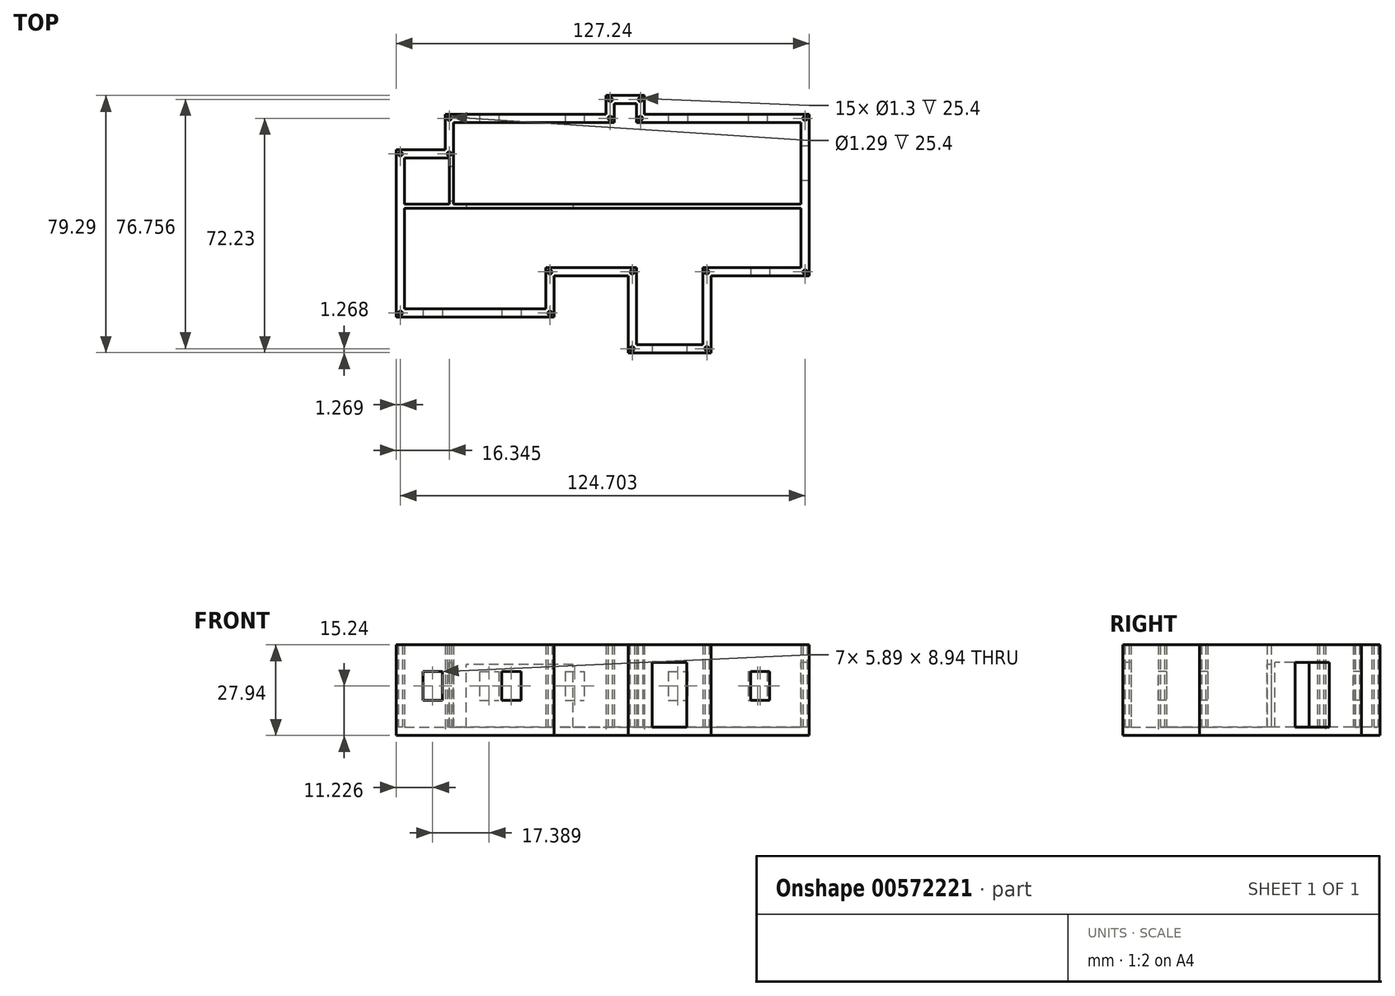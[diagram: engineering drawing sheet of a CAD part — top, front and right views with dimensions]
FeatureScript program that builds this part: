
annotation { "Feature Type Name" : "Feature", "Feature Type Description" : "" }
export const myFeature = defineFeature(function(context is Context, id is Id, definition is map)
    precondition{}
    {
        {
            var Q0;
            Q0=qCreatedBy(makeId("Top.planeOp"),FACE);
            var sketch = newSketch(context, id + "F0", { "sketchPlane" : qUnion([Q0])});
            skLineSegment(sketch, "E0", {"start": v(-47.94, 2.54) * mm, "end": v(1.67, 2.54) * mm});
            skLineSegment(sketch, "E1", {"start": v(1.67, 2.54) * mm, "end": v(1.67, 8.33) * mm});
            skLineSegment(sketch, "E2", {"start": v(1.67, 8.33) * mm, "end": v(13.5, 8.33) * mm});
            skLineSegment(sketch, "E3", {"start": v(13.5, 8.33) * mm, "end": v(13.5, 2.54) * mm});
            skLineSegment(sketch, "E4", {"start": v(13.5, 2.54) * mm, "end": v(64.22, 2.54) * mm});
            skLineSegment(sketch, "E5", {"start": v(-47.94, 2.54) * mm, "end": v(-47.94, -8.42) * mm});
            skLineSegment(sketch, "E6", {"start": v(-47.94, -8.42) * mm, "end": v(-63.02, -8.42) * mm});
            skLineSegment(sketch, "E7", {"start": v(-63.02, -8.42) * mm, "end": v(-63.02, -60.04) * mm});
            skLineSegment(sketch, "E8", {"start": v(-63.02, -60.04) * mm, "end": v(-14.4, -60.04) * mm});
            skLineSegment(sketch, "E9", {"start": v(-14.4, -60.04) * mm, "end": v(-14.4, -47.34) * mm});
            skLineSegment(sketch, "E10", {"start": v(-14.4, -47.34) * mm, "end": v(8.42, -47.34) * mm});
            skLineSegment(sketch, "E11", {"start": v(8.42, -47.34) * mm, "end": v(8.42, -70.96) * mm});
            skLineSegment(sketch, "E12", {"start": v(8.42, -70.96) * mm, "end": v(33.96, -70.96) * mm});
            skLineSegment(sketch, "E13", {"start": v(33.96, -70.96) * mm, "end": v(33.96, -47.34) * mm});
            skLineSegment(sketch, "E14", {"start": v(33.96, -47.34) * mm, "end": v(64.22, -47.34) * mm});
            skLineSegment(sketch, "E15", {"start": v(64.22, -47.34) * mm, "end": v(64.22, 2.54) * mm});
            skLineSegment(sketch, "E16", {"start": v(10.96, -47.34) * mm, "end": v(10.96, -68.42) * mm});
            skLineSegment(sketch, "E17", {"start": v(10.96, -68.42) * mm, "end": v(31.42, -68.42) * mm});
            skLineSegment(sketch, "E18", {"start": v(31.42, -68.42) * mm, "end": v(31.42, -44.8) * mm});
            skLineSegment(sketch, "E19", {"start": v(31.42, -44.8) * mm, "end": v(61.68, -44.8) * mm});
            skLineSegment(sketch, "E20", {"start": v(61.68, -44.8) * mm, "end": v(61.68, 0) * mm});
            skLineSegment(sketch, "E21", {"start": v(61.68, 0) * mm, "end": v(10.96, 0) * mm});
            skLineSegment(sketch, "E22", {"start": v(10.96, 0) * mm, "end": v(10.96, 5.8) * mm});
            skLineSegment(sketch, "E23", {"start": v(10.96, 5.8) * mm, "end": v(4.2, 5.8) * mm});
            skLineSegment(sketch, "E24", {"start": v(4.2, 5.8) * mm, "end": v(4.2, 0) * mm});
            skLineSegment(sketch, "E25", {"start": v(4.2, 0) * mm, "end": v(-45.4, 0) * mm});
            skLineSegment(sketch, "E26", {"start": v(-45.4, 0) * mm, "end": v(-45.4, -10.96) * mm});
            skLineSegment(sketch, "E27", {"start": v(-45.4, -10.96) * mm, "end": v(-60.48, -10.96) * mm});
            skLineSegment(sketch, "E28", {"start": v(-60.48, -10.96) * mm, "end": v(-60.48, -57.5) * mm});
            skLineSegment(sketch, "E29", {"start": v(-60.48, -57.5) * mm, "end": v(-16.95, -57.5) * mm});
            skLineSegment(sketch, "E30", {"start": v(-16.95, -57.5) * mm, "end": v(-16.95, -44.8) * mm});
            skLineSegment(sketch, "E31", {"start": v(-16.95, -44.8) * mm, "end": v(10.96, -44.8) * mm});
            skLineSegment(sketch, "E32", {"start": v(10.96, -44.8) * mm, "end": v(10.96, -47.34) * mm});
            skLineSegment(sketch, "E33", {"start": v(-60.48, -26.49) * mm, "end": v(61.68, -26.49) * mm});
            skLineSegment(sketch, "E34", {"start": v(-60.48, -25.22) * mm, "end": v(61.68, -25.22) * mm});
            skLineSegment(sketch, "E35", {"start": v(-45.4, -10.96) * mm, "end": v(-45.4, -25.22) * mm});
            skLineSegment(sketch, "E36", {"start": v(-46.67, -10.96) * mm, "end": v(-46.67, -25.22) * mm});
            skLineSegment(sketch, "E37.top", {"start": v(31.42, -70.96) * mm, "end": v(33.96, -70.96) * mm});
            skLineSegment(sketch, "E37.right", {"start": v(33.96, -68.42) * mm, "end": v(33.96, -70.96) * mm});
            skLineSegment(sketch, "E38.top", {"start": v(61.68, 2.54) * mm, "end": v(64.22, 2.54) * mm});
            skLineSegment(sketch, "E38.right", {"start": v(64.22, 0) * mm, "end": v(64.22, 2.54) * mm});
            skLineSegment(sketch, "E39.top", {"start": v(-45.4, 2.54) * mm, "end": v(-47.94, 2.54) * mm});
            skLineSegment(sketch, "E39.right", {"start": v(-47.94, 0) * mm, "end": v(-47.94, 2.54) * mm});
            skLineSegment(sketch, "E40.bottom", {"start": v(-63.02, -60.04) * mm, "end": v(-60.48, -60.04) * mm});
            skLineSegment(sketch, "E40.left", {"start": v(-63.02, -60.04) * mm, "end": v(-63.02, -57.5) * mm});
            skLineSegment(sketch, "E41.top", {"start": v(-60.48, -8.42) * mm, "end": v(-63.02, -8.42) * mm});
            skLineSegment(sketch, "E41.right", {"start": v(-63.02, -10.96) * mm, "end": v(-63.02, -8.42) * mm});
            skLineSegment(sketch, "E42.top", {"start": v(61.68, -47.34) * mm, "end": v(64.22, -47.34) * mm});
            skLineSegment(sketch, "E42.right", {"start": v(64.22, -44.8) * mm, "end": v(64.22, -47.34) * mm});
            skLineSegment(sketch, "E43.top", {"start": v(33.96, -44.8) * mm, "end": v(31.42, -44.8) * mm});
            skLineSegment(sketch, "E43.right", {"start": v(31.42, -47.34) * mm, "end": v(31.42, -44.8) * mm});
            skLineSegment(sketch, "E44.bottom", {"start": v(8.42, -70.96) * mm, "end": v(10.96, -70.96) * mm});
            skLineSegment(sketch, "E44.left", {"start": v(8.42, -70.96) * mm, "end": v(8.42, -68.42) * mm});
            skLineSegment(sketch, "E45.top", {"start": v(8.42, -44.8) * mm, "end": v(10.96, -44.8) * mm});
            skLineSegment(sketch, "E45.right", {"start": v(10.96, -47.34) * mm, "end": v(10.96, -44.8) * mm});
            skLineSegment(sketch, "E46.top", {"start": v(-14.4, -44.8) * mm, "end": v(-16.95, -44.8) * mm});
            skLineSegment(sketch, "E46.right", {"start": v(-16.95, -47.34) * mm, "end": v(-16.95, -44.8) * mm});
            skLineSegment(sketch, "E47.bottom", {"start": v(13.5, 8.33) * mm, "end": v(10.96, 8.33) * mm});
            skLineSegment(sketch, "E47.left", {"start": v(13.5, 8.33) * mm, "end": v(13.5, 5.8) * mm});
            skLineSegment(sketch, "E48.bottom", {"start": v(1.67, 8.33) * mm, "end": v(4.2, 8.33) * mm});
            skLineSegment(sketch, "E48.left", {"start": v(1.67, 8.33) * mm, "end": v(1.67, 5.8) * mm});
            skLineSegment(sketch, "E49.top", {"start": v(1.67, 0) * mm, "end": v(4.2, 0) * mm});
            skLineSegment(sketch, "E49.right", {"start": v(4.2, 2.54) * mm, "end": v(4.2, 0) * mm});
            skLineSegment(sketch, "E50.bottom", {"start": v(10.96, 0) * mm, "end": v(13.5, 0) * mm});
            skLineSegment(sketch, "E50.left", {"start": v(10.96, 0) * mm, "end": v(10.96, 2.54) * mm});
            skLineSegment(sketch, "E51.bottom", {"start": v(-14.4, -60.04) * mm, "end": v(-16.95, -60.04) * mm});
            skLineSegment(sketch, "E51.left", {"start": v(-14.4, -60.04) * mm, "end": v(-14.4, -57.5) * mm});
            skLineSegment(sketch, "E52.top", {"start": v(-47.94, -10.96) * mm, "end": v(-45.4, -10.96) * mm});
            skLineSegment(sketch, "E52.right", {"start": v(-45.4, -8.42) * mm, "end": v(-45.4, -10.96) * mm});
            skCircle(sketch, "E53", {"center": v(-61.75, -9.69) * mm, "radius": 0.65 * mm});
            skPoint(sketch, "E53.centerSnap0", {"position": v(-63.02, -9.69) * mm});
            skPoint(sketch, "E53.centerSnap1", {"position": v(-61.75, -10.96) * mm});
            skCircle(sketch, "E54", {"center": v(-46.67, 1.27) * mm, "radius": 0.64 * mm});
            skPoint(sketch, "E54.centerSnap0", {"position": v(-46.67, 0) * mm});
            skPoint(sketch, "E54.centerSnap1", {"position": v(-47.94, 1.27) * mm});
            skCircle(sketch, "E55", {"center": v(-46.67, -9.69) * mm, "radius": 0.65 * mm});
            skPoint(sketch, "E55.centerSnap0", {"position": v(-47.94, -9.69) * mm});
            skCircle(sketch, "E56", {"center": v(-61.75, -58.77) * mm, "radius": 0.65 * mm});
            skPoint(sketch, "E56.centerSnap0", {"position": v(-61.75, -60.04) * mm});
            skPoint(sketch, "E56.centerSnap1", {"position": v(-60.48, -58.77) * mm});
            skCircle(sketch, "E57", {"center": v(-15.68, -58.77) * mm, "radius": 0.65 * mm});
            skPoint(sketch, "E57.centerSnap0", {"position": v(-15.68, -60.04) * mm});
            skPoint(sketch, "E57.centerSnap1", {"position": v(-14.4, -58.77) * mm});
            skCircle(sketch, "E58", {"center": v(-15.68, -46.07) * mm, "radius": 0.65 * mm});
            skPoint(sketch, "E58.centerSnap0", {"position": v(-16.95, -46.07) * mm});
            skPoint(sketch, "E58.centerSnap1", {"position": v(-15.68, -47.34) * mm});
            skCircle(sketch, "E59", {"center": v(9.69, -46.07) * mm, "radius": 0.65 * mm});
            skPoint(sketch, "E59.centerSnap0", {"position": v(9.69, -47.34) * mm});
            skPoint(sketch, "E59.centerSnap1", {"position": v(10.96, -46.07) * mm});
            skCircle(sketch, "E60", {"center": v(9.69, -69.7) * mm, "radius": 0.65 * mm});
            skPoint(sketch, "E60.centerSnap0", {"position": v(9.69, -70.96) * mm});
            skPoint(sketch, "E60.centerSnap1", {"position": v(8.42, -69.7) * mm});
            skCircle(sketch, "E61", {"center": v(32.7, -69.7) * mm, "radius": 0.65 * mm});
            skPoint(sketch, "E61.centerSnap0", {"position": v(32.7, -70.96) * mm});
            skPoint(sketch, "E61.centerSnap1", {"position": v(31.42, -69.7) * mm});
            skCircle(sketch, "E62", {"center": v(32.7, -46.07) * mm, "radius": 0.65 * mm});
            skPoint(sketch, "E62.centerSnap0", {"position": v(32.7, -47.34) * mm});
            skPoint(sketch, "E62.centerSnap1", {"position": v(31.42, -46.07) * mm});
            skCircle(sketch, "E63", {"center": v(62.95, -46.07) * mm, "radius": 0.65 * mm});
            skPoint(sketch, "E63.centerSnap0", {"position": v(61.68, -46.07) * mm});
            skPoint(sketch, "E63.centerSnap1", {"position": v(62.95, -47.34) * mm});
            skCircle(sketch, "E64", {"center": v(62.95, 1.27) * mm, "radius": 0.65 * mm});
            skPoint(sketch, "E64.centerSnap0", {"position": v(62.95, 0) * mm});
            skPoint(sketch, "E64.centerSnap1", {"position": v(64.22, 1.27) * mm});
            skCircle(sketch, "E65", {"center": v(12.23, 1.27) * mm, "radius": 0.65 * mm});
            skPoint(sketch, "E65.centerSnap0", {"position": v(12.23, 0) * mm});
            skPoint(sketch, "E65.centerSnap1", {"position": v(13.5, 1.27) * mm});
            skCircle(sketch, "E66", {"center": v(12.23, 7.06) * mm, "radius": 0.65 * mm});
            skPoint(sketch, "E66.centerSnap0", {"position": v(13.5, 7.06) * mm});
            skPoint(sketch, "E66.centerSnap1", {"position": v(12.23, 5.8) * mm});
            skCircle(sketch, "E67", {"center": v(2.94, 7.06) * mm, "radius": 0.65 * mm});
            skPoint(sketch, "E67.centerSnap0", {"position": v(4.2, 7.06) * mm});
            skPoint(sketch, "E67.centerSnap1", {"position": v(2.94, 5.8) * mm});
            skCircle(sketch, "E68", {"center": v(2.94, 1.27) * mm, "radius": 0.65 * mm});
            skPoint(sketch, "E68.centerSnap0", {"position": v(4.2, 1.27) * mm});
            skPoint(sketch, "E68.centerSnap1", {"position": v(2.94, 0) * mm});
            skSolve(sketch);
        }
        {
            var Q0;
            Q0=sQuery(id+"F0.wireOp",EDGE,"E54");
            var Q1;
            Q1=sQuery(id+"F0.wireOp",EDGE,"E55");
            var Q2;
            Q2=sQuery(id+"F0.wireOp",EDGE,"E53");
            var Q3;
            Q3=sQuery(id+"F0.wireOp",EDGE,"E56");
            var Q4;
            Q4=sQuery(id+"F0.wireOp",EDGE,"E57");
            var Q5;
            Q5=sQuery(id+"F0.wireOp",EDGE,"E58");
            var Q6;
            Q6=sQuery(id+"F0.wireOp",EDGE,"E59");
            var Q7;
            Q7=sQuery(id+"F0.wireOp",EDGE,"E60");
            var Q8;
            Q8=sQuery(id+"F0.wireOp",EDGE,"E61");
            var Q9;
            Q9=sQuery(id+"F0.wireOp",EDGE,"E62");
            var Q10;
            Q10=sQuery(id+"F0.wireOp",EDGE,"E63");
            var Q11;
            Q11=sQuery(id+"F0.wireOp",EDGE,"E64");
            var Q12;
            Q12=sQuery(id+"F0.wireOp",EDGE,"E65");
            var Q13;
            Q13=sQuery(id+"F0.wireOp",EDGE,"E66");
            var Q14;
            Q14=sQuery(id+"F0.wireOp",EDGE,"E67");
            var Q15;
            Q15=sQuery(id+"F0.wireOp",EDGE,"E68");
            extrude(context, id + "F1", {"bodyType" : ToolBodyType.SURFACE, "surfaceEntities" : qUnion([Q0, Q1, Q2, Q3, Q4, Q5, Q6, Q7, Q8, Q9, Q10, Q11, Q12, Q13, Q14, Q15]), "depth" : 27.94 * mm, "offsetDistance" : 25.4 * mm});
        }
        {
            var Q0;
            {var subQ0=sQuery(id+"F0.wireOp",EDGE,"E35");Q0=makeQuery(id+"F0.imprint","IMPRINT",FACE,{"disambiguationData":[TD([[makeQuery(id+"F0.imprint","IMPRINT",EDGE,{"derivedFrom":subQ0}),-1.0]])]});}
            var Q1;
            {var subQ4=sQuery(id+"F0.wireOp",EDGE,"E33");Q1=makeQuery(id+"F0.imprint","IMPRINT",FACE,{"disambiguationData":[TD([[makeQuery(id+"F0.imprint","IMPRINT",EDGE,{"derivedFrom":subQ4}),1.0]])]});}
            var Q2;
            Q2=makeQuery(id+"F0.imprint","IMPRINT",FACE,{"disambiguationData":[TD([[makeQuery(id+"F0.imprint","IMPRINT",EDGE,{"derivedFrom":sQuery(id+"F0.wireOp",EDGE,"E0")}),-1.0]])]});
            extrude(context, id + "F2", {"entities" : qUnion([Q0, Q1, Q2]), "depth" : 25.4 * mm, "offsetDistance" : 25.4 * mm});
        }
        {
            var Q0;
            Q0=makeQuery(id+"F2.opExtrude","SWEPT_FACE",FACE,{"disambiguationData":[OSD([sQuery(id+"F0.wireOp",EDGE,"E25"),sQuery(id+"F0.wireOp",EDGE,"E49.top")])]});
            var sketch = newSketch(context, id + "F3", { "sketchPlane" : qUnion([Q0])});
            skLineSegment(sketch, "E69.bottom", {"start": v(-31.46, 8.23) * mm, "end": v(-37.35, 8.23) * mm});
            skLineSegment(sketch, "E69.top", {"start": v(-31.46, 17.17) * mm, "end": v(-37.35, 17.17) * mm});
            skLineSegment(sketch, "E69.left", {"start": v(-31.46, 8.23) * mm, "end": v(-31.46, 17.17) * mm});
            skLineSegment(sketch, "E69.right", {"start": v(-37.35, 8.23) * mm, "end": v(-37.35, 17.17) * mm});
            skPoint(sketch, "E69.middle", {"position": v(-34.4, 12.7) * mm});
            skLineSegment(sketch, "E70.bottom", {"start": v(-5.05, 8.23) * mm, "end": v(-10.94, 8.23) * mm});
            skLineSegment(sketch, "E70.top", {"start": v(-5.05, 17.17) * mm, "end": v(-10.94, 17.17) * mm});
            skLineSegment(sketch, "E70.left", {"start": v(-5.05, 8.23) * mm, "end": v(-5.05, 17.17) * mm});
            skLineSegment(sketch, "E70.right", {"start": v(-10.94, 8.23) * mm, "end": v(-10.94, 17.17) * mm});
            skPoint(sketch, "E70.middle", {"position": v(-8, 12.7) * mm});
            skSolve(sketch);
        }
        {
            var Q0;
            Q0=makeQuery(id+"F2.opExtrude","SWEPT_FACE",FACE,{"disambiguationData":[OSD([sQuery(id+"F0.wireOp",EDGE,"E21"),sQuery(id+"F0.wireOp",EDGE,"E50.bottom")])]});
            var sketch = newSketch(context, id + "F4", { "sketchPlane" : qUnion([Q0])});
            skLineSegment(sketch, "E71.bottom", {"start": v(26.71, 8.23) * mm, "end": v(20.82, 8.23) * mm});
            skLineSegment(sketch, "E71.top", {"start": v(26.71, 17.17) * mm, "end": v(20.82, 17.17) * mm});
            skLineSegment(sketch, "E71.left", {"start": v(26.71, 8.23) * mm, "end": v(26.71, 17.17) * mm});
            skLineSegment(sketch, "E71.right", {"start": v(20.82, 8.23) * mm, "end": v(20.82, 17.17) * mm});
            skPoint(sketch, "E71.middle", {"position": v(23.76, 12.7) * mm});
            skLineSegment(sketch, "E72.bottom", {"start": v(51.31, 8.23) * mm, "end": v(45.42, 8.23) * mm});
            skLineSegment(sketch, "E72.top", {"start": v(51.31, 17.17) * mm, "end": v(45.42, 17.17) * mm});
            skLineSegment(sketch, "E72.left", {"start": v(51.31, 8.23) * mm, "end": v(51.31, 17.17) * mm});
            skLineSegment(sketch, "E72.right", {"start": v(45.42, 8.23) * mm, "end": v(45.42, 17.17) * mm});
            skPoint(sketch, "E72.middle", {"position": v(48.36, 12.7) * mm});
            skSolve(sketch);
        }
        {
            var Q0;
            Q0=makeQuery(id+"F2.opExtrude","SWEPT_FACE",FACE,{"disambiguationData":[OSD([sQuery(id+"F0.wireOp",EDGE,"E12"),sQuery(id+"F0.wireOp",EDGE,"E37.top"),sQuery(id+"F0.wireOp",EDGE,"E44.bottom")])]});
            var sketch = newSketch(context, id + "F5", { "sketchPlane" : qUnion([Q0])});
            skLineSegment(sketch, "E73.bottom", {"start": v(26.49, 0) * mm, "end": v(15.9, 0) * mm});
            skLineSegment(sketch, "E73.top", {"start": v(26.49, 19.94) * mm, "end": v(15.9, 19.94) * mm});
            skLineSegment(sketch, "E73.left", {"start": v(26.49, 0) * mm, "end": v(26.49, 19.94) * mm});
            skLineSegment(sketch, "E73.right", {"start": v(15.9, 0) * mm, "end": v(15.9, 19.94) * mm});
            skPoint(sketch, "E73.middle", {"position": v(21.19, 9.97) * mm});
            skSolve(sketch);
        }
        {
            var Q0;
            Q0=makeQuery(id+"F2.opExtrude","SWEPT_FACE",FACE,{"disambiguationData":[OSD([sQuery(id+"F0.wireOp",EDGE,"E14"),sQuery(id+"F0.wireOp",EDGE,"E42.top")])]});
            var sketch = newSketch(context, id + "F6", { "sketchPlane" : qUnion([Q0])});
            skLineSegment(sketch, "E74.bottom", {"start": v(52.04, 8.23) * mm, "end": v(46.15, 8.23) * mm});
            skLineSegment(sketch, "E74.top", {"start": v(52.04, 17.17) * mm, "end": v(46.15, 17.17) * mm});
            skLineSegment(sketch, "E74.left", {"start": v(52.04, 8.23) * mm, "end": v(52.04, 17.17) * mm});
            skLineSegment(sketch, "E74.right", {"start": v(46.15, 8.23) * mm, "end": v(46.15, 17.17) * mm});
            skPoint(sketch, "E74.middle", {"position": v(49.1, 12.7) * mm});
            skSolve(sketch);
        }
        {
            var Q0;
            Q0=makeQuery(id+"F2.opExtrude","SWEPT_FACE",FACE,{"disambiguationData":[OSD([sQuery(id+"F0.wireOp",EDGE,"E8"),sQuery(id+"F0.wireOp",EDGE,"E40.bottom"),sQuery(id+"F0.wireOp",EDGE,"E51.bottom")])]});
            var sketch = newSketch(context, id + "F7", { "sketchPlane" : qUnion([Q0])});
            skLineSegment(sketch, "E75.bottom", {"start": v(-24.6, 8.23) * mm, "end": v(-30.49, 8.23) * mm});
            skLineSegment(sketch, "E75.top", {"start": v(-24.6, 17.17) * mm, "end": v(-30.49, 17.17) * mm});
            skLineSegment(sketch, "E75.left", {"start": v(-24.6, 8.23) * mm, "end": v(-24.6, 17.17) * mm});
            skLineSegment(sketch, "E75.right", {"start": v(-30.49, 8.23) * mm, "end": v(-30.49, 17.17) * mm});
            skPoint(sketch, "E75.middle", {"position": v(-27.54, 12.7) * mm});
            skLineSegment(sketch, "E76.bottom", {"start": v(-48.85, 8.23) * mm, "end": v(-54.74, 8.23) * mm});
            skLineSegment(sketch, "E76.top", {"start": v(-48.85, 17.17) * mm, "end": v(-54.74, 17.17) * mm});
            skLineSegment(sketch, "E76.left", {"start": v(-48.85, 8.23) * mm, "end": v(-48.85, 17.17) * mm});
            skLineSegment(sketch, "E76.right", {"start": v(-54.74, 8.23) * mm, "end": v(-54.74, 17.17) * mm});
            skPoint(sketch, "E76.middle", {"position": v(-51.8, 12.7) * mm});
            skSolve(sketch);
        }
        {
            var Q0;
            Q0=makeQuery(id+"F2.opExtrude","SWEPT_FACE",FACE,{"disambiguationData":[OSD([sQuery(id+"F0.wireOp",EDGE,"E33")])]});
            var sketch = newSketch(context, id + "F8", { "sketchPlane" : qUnion([Q0])});
            skLineSegment(sketch, "E77.bottom", {"start": v(-8.5, 0) * mm, "end": v(-41.46, 0) * mm});
            skLineSegment(sketch, "E77.top", {"start": v(-8.5, 19.34) * mm, "end": v(-41.46, 19.34) * mm});
            skLineSegment(sketch, "E77.left", {"start": v(-8.5, 0) * mm, "end": v(-8.5, 19.34) * mm});
            skLineSegment(sketch, "E77.right", {"start": v(-41.46, 0) * mm, "end": v(-41.46, 19.34) * mm});
            skPoint(sketch, "E77.middle", {"position": v(-24.98, 9.67) * mm});
            skSolve(sketch);
        }
        {
            var Q0;
            {var subQ0=sQuery(id+"F0.wireOp",EDGE,"E20");Q0=makeQuery(id+"F2.opExtrude","SWEPT_FACE",FACE,{"disambiguationData":[OSD([subQ0]),TDD([makeQuery(id+"F0.imprint","IMPRINT",EDGE,{"disambiguationData":[TD([[makeQuery(id+"F0.imprint","INTERSECT",VERTEX,{"derivedFrom":[subQ0,sQuery(id+"F0.wireOp",EDGE,"E21")]}),1.0]])],"derivedFrom":subQ0})])]});}
            var sketch = newSketch(context, id + "F9", { "sketchPlane" : qUnion([Q0])});
            skLineSegment(sketch, "E78.bottom", {"start": v(17.9, 0) * mm, "end": v(7.31, 0) * mm});
            skLineSegment(sketch, "E78.top", {"start": v(17.9, 19.94) * mm, "end": v(7.31, 19.94) * mm});
            skLineSegment(sketch, "E78.left", {"start": v(17.9, 0) * mm, "end": v(17.9, 19.94) * mm});
            skLineSegment(sketch, "E78.right", {"start": v(7.31, 0) * mm, "end": v(7.31, 19.94) * mm});
            skPoint(sketch, "E78.middle", {"position": v(12.6, 9.97) * mm});
            skSolve(sketch);
        }
        {
            var Q0;
            Q0=makeQuery(id+"F2.opExtrude","SWEPT_FACE",FACE,{"disambiguationData":[OSD([sQuery(id+"F0.wireOp",EDGE,"E26"),sQuery(id+"F0.wireOp",EDGE,"E35"),sQuery(id+"F0.wireOp",EDGE,"E52.right")])]});
            var sketch = newSketch(context, id + "F10", { "sketchPlane" : qUnion([Q0])});
            skLineSegment(sketch, "E79.bottom", {"start": v(-13.52, 0) * mm, "end": v(-24.11, 0) * mm});
            skLineSegment(sketch, "E79.top", {"start": v(-13.52, 19.94) * mm, "end": v(-24.11, 19.94) * mm});
            skLineSegment(sketch, "E79.left", {"start": v(-13.52, 0) * mm, "end": v(-13.52, 19.94) * mm});
            skLineSegment(sketch, "E79.right", {"start": v(-24.11, 0) * mm, "end": v(-24.11, 19.94) * mm});
            skPoint(sketch, "E79.middle", {"position": v(-18.81, 9.97) * mm});
            skSolve(sketch);
        }
        {
            var Q0;
            Q0=makeQuery(id+"F2.opExtrude","CAP_FACE",FACE,{"disambiguationData":[OSD([sQuery(id+"F0.wireOp",EDGE,"E0"),sQuery(id+"F0.wireOp",EDGE,"E1"),sQuery(id+"F0.wireOp",EDGE,"E2"),sQuery(id+"F0.wireOp",EDGE,"E3"),sQuery(id+"F0.wireOp",EDGE,"E4"),sQuery(id+"F0.wireOp",EDGE,"E5"),sQuery(id+"F0.wireOp",EDGE,"E6"),sQuery(id+"F0.wireOp",EDGE,"E7"),sQuery(id+"F0.wireOp",EDGE,"E8"),sQuery(id+"F0.wireOp",EDGE,"E9"),sQuery(id+"F0.wireOp",EDGE,"E10"),sQuery(id+"F0.wireOp",EDGE,"E11"),sQuery(id+"F0.wireOp",EDGE,"E12"),sQuery(id+"F0.wireOp",EDGE,"E13"),sQuery(id+"F0.wireOp",EDGE,"E14"),sQuery(id+"F0.wireOp",EDGE,"E15"),sQuery(id+"F0.wireOp",EDGE,"E16"),sQuery(id+"F0.wireOp",EDGE,"E17"),sQuery(id+"F0.wireOp",EDGE,"E18"),sQuery(id+"F0.wireOp",EDGE,"E19"),sQuery(id+"F0.wireOp",EDGE,"E20"),sQuery(id+"F0.wireOp",EDGE,"E21"),sQuery(id+"F0.wireOp",EDGE,"E22"),sQuery(id+"F0.wireOp",EDGE,"E23"),sQuery(id+"F0.wireOp",EDGE,"E24"),sQuery(id+"F0.wireOp",EDGE,"E25"),sQuery(id+"F0.wireOp",EDGE,"E26"),sQuery(id+"F0.wireOp",EDGE,"E27"),sQuery(id+"F0.wireOp",EDGE,"E28"),sQuery(id+"F0.wireOp",EDGE,"E29"),sQuery(id+"F0.wireOp",EDGE,"E30"),sQuery(id+"F0.wireOp",EDGE,"E31"),sQuery(id+"F0.wireOp",EDGE,"E33"),sQuery(id+"F0.wireOp",EDGE,"E34"),sQuery(id+"F0.wireOp",EDGE,"E35"),sQuery(id+"F0.wireOp",EDGE,"E36"),sQuery(id+"F0.wireOp",EDGE,"E37.top"),sQuery(id+"F0.wireOp",EDGE,"E37.right"),sQuery(id+"F0.wireOp",EDGE,"E38.top"),sQuery(id+"F0.wireOp",EDGE,"E38.right"),sQuery(id+"F0.wireOp",EDGE,"E39.top"),sQuery(id+"F0.wireOp",EDGE,"E39.right"),sQuery(id+"F0.wireOp",EDGE,"E40.bottom"),sQuery(id+"F0.wireOp",EDGE,"E40.left"),sQuery(id+"F0.wireOp",EDGE,"E41.top"),sQuery(id+"F0.wireOp",EDGE,"E41.right"),sQuery(id+"F0.wireOp",EDGE,"E42.top"),sQuery(id+"F0.wireOp",EDGE,"E42.right"),sQuery(id+"F0.wireOp",EDGE,"E43.top"),sQuery(id+"F0.wireOp",EDGE,"E43.right"),sQuery(id+"F0.wireOp",EDGE,"E44.bottom"),sQuery(id+"F0.wireOp",EDGE,"E44.left"),sQuery(id+"F0.wireOp",EDGE,"E45.top"),sQuery(id+"F0.wireOp",EDGE,"E45.right"),sQuery(id+"F0.wireOp",EDGE,"E46.top"),sQuery(id+"F0.wireOp",EDGE,"E46.right"),sQuery(id+"F0.wireOp",EDGE,"E47.bottom"),sQuery(id+"F0.wireOp",EDGE,"E47.left"),sQuery(id+"F0.wireOp",EDGE,"E48.bottom"),sQuery(id+"F0.wireOp",EDGE,"E48.left"),sQuery(id+"F0.wireOp",EDGE,"E49.top"),sQuery(id+"F0.wireOp",EDGE,"E49.right"),sQuery(id+"F0.wireOp",EDGE,"E50.bottom"),sQuery(id+"F0.wireOp",EDGE,"E50.left"),sQuery(id+"F0.wireOp",EDGE,"E51.bottom"),sQuery(id+"F0.wireOp",EDGE,"E51.left"),sQuery(id+"F0.wireOp",EDGE,"E52.top"),sQuery(id+"F0.wireOp",EDGE,"E52.right"),sQuery(id+"F0.wireOp",EDGE,"E53"),sQuery(id+"F0.wireOp",EDGE,"E54"),sQuery(id+"F0.wireOp",EDGE,"E55"),sQuery(id+"F0.wireOp",EDGE,"E56"),sQuery(id+"F0.wireOp",EDGE,"E57"),sQuery(id+"F0.wireOp",EDGE,"E58"),sQuery(id+"F0.wireOp",EDGE,"E59"),sQuery(id+"F0.wireOp",EDGE,"E60"),sQuery(id+"F0.wireOp",EDGE,"E61"),sQuery(id+"F0.wireOp",EDGE,"E62"),sQuery(id+"F0.wireOp",EDGE,"E63"),sQuery(id+"F0.wireOp",EDGE,"E64"),sQuery(id+"F0.wireOp",EDGE,"E65"),sQuery(id+"F0.wireOp",EDGE,"E66"),sQuery(id+"F0.wireOp",EDGE,"E67"),sQuery(id+"F0.wireOp",EDGE,"E68")])],"isStart":true});
            var sketch = newSketch(context, id + "F11", { "sketchPlane" : qUnion([Q0])});
            skLineSegment(sketch, "E80.0", {"start": v(13.5, -2.54) * mm, "end": v(64.22, -2.54) * mm});
            skLineSegment(sketch, "E81.0", {"start": v(64.22, -2.54) * mm, "end": v(64.22, 47.34) * mm});
            skLineSegment(sketch, "E82.0", {"start": v(33.96, 47.34) * mm, "end": v(64.22, 47.34) * mm});
            skLineSegment(sketch, "E83.0", {"start": v(33.96, 47.34) * mm, "end": v(33.96, 70.96) * mm});
            skLineSegment(sketch, "E84.0", {"start": v(8.42, 70.96) * mm, "end": v(33.96, 70.96) * mm});
            skLineSegment(sketch, "E85.0", {"start": v(8.42, 47.34) * mm, "end": v(8.42, 70.96) * mm});
            skLineSegment(sketch, "E86.0", {"start": v(-14.4, 47.34) * mm, "end": v(8.42, 47.34) * mm});
            skLineSegment(sketch, "E87.0", {"start": v(-14.4, 60.04) * mm, "end": v(-14.4, 47.34) * mm});
            skLineSegment(sketch, "E88.0", {"start": v(-63.02, 60.04) * mm, "end": v(-14.4, 60.04) * mm});
            skLineSegment(sketch, "E89.0", {"start": v(-63.02, 60.04) * mm, "end": v(-63.02, 8.42) * mm});
            skLineSegment(sketch, "E90.0", {"start": v(-47.94, 8.42) * mm, "end": v(-63.02, 8.42) * mm});
            skLineSegment(sketch, "E91.0", {"start": v(-47.94, 8.42) * mm, "end": v(-47.94, -2.54) * mm});
            skLineSegment(sketch, "E92.0", {"start": v(-47.94, -2.54) * mm, "end": v(1.67, -2.54) * mm});
            skLineSegment(sketch, "E93.0", {"start": v(1.67, -8.33) * mm, "end": v(1.67, -2.54) * mm});
            skLineSegment(sketch, "E94.0", {"start": v(13.5, -8.33) * mm, "end": v(1.67, -8.33) * mm});
            skLineSegment(sketch, "E95.0", {"start": v(13.5, -8.33) * mm, "end": v(13.5, -2.54) * mm});
            skSolve(sketch);
        }
        {
            var Q0;
            Q0 = qSketchRegion(id + "F11", true);
            extrude(context, id + "F12", {"entities" : qUnion([Q0]), "operationType" : NewBodyOperationType.ADD, "depth" : 2.54 * mm, "offsetDistance" : 25.4 * mm});
        }
        {
            var Q0;
            Q0=makeQuery(id+"F4.imprint","IMPRINT",FACE,{"disambiguationData":[TD([[makeQuery(id+"F4.imprint","IMPRINT",EDGE,{"derivedFrom":sQuery(id+"F4.wireOp",EDGE,"E72.bottom")}),-1.0]])]});
            var Q1;
            Q1=makeQuery(id+"F4.imprint","IMPRINT",FACE,{"disambiguationData":[TD([[makeQuery(id+"F4.imprint","IMPRINT",EDGE,{"derivedFrom":sQuery(id+"F4.wireOp",EDGE,"E71.bottom")}),-1.0]])]});
            var Q2;
            Q2=makeQuery(id+"F3.imprint","IMPRINT",FACE,{"disambiguationData":[TD([[makeQuery(id+"F3.imprint","IMPRINT",EDGE,{"derivedFrom":sQuery(id+"F3.wireOp",EDGE,"E70.bottom")}),-1.0]])]});
            var Q3;
            Q3=makeQuery(id+"F3.imprint","IMPRINT",FACE,{"disambiguationData":[TD([[makeQuery(id+"F3.imprint","IMPRINT",EDGE,{"derivedFrom":sQuery(id+"F3.wireOp",EDGE,"E69.bottom")}),-1.0]])]});
            extrude(context, id + "F13", {"entities" : qUnion([Q0, Q1, Q2, Q3]), "operationType" : NewBodyOperationType.REMOVE, "oppositeDirection" : true, "depth" : 25.4 * mm, "offsetDistance" : 25.4 * mm});
        }
        {
            var Q0;
            Q0=makeQuery(id+"F6.imprint","IMPRINT",FACE,{"disambiguationData":[TD([[makeQuery(id+"F6.imprint","IMPRINT",EDGE,{"derivedFrom":sQuery(id+"F6.wireOp",EDGE,"E74.bottom")}),-1.0]])]});
            var Q1;
            Q1=makeQuery(id+"F5.imprint","IMPRINT",FACE,{"disambiguationData":[TD([[makeQuery(id+"F5.imprint","IMPRINT",EDGE,{"derivedFrom":sQuery(id+"F5.wireOp",EDGE,"E73.bottom")}),1.0]])]});
            var Q2;
            Q2=makeQuery(id+"F7.imprint","IMPRINT",FACE,{"disambiguationData":[TD([[makeQuery(id+"F7.imprint","IMPRINT",EDGE,{"derivedFrom":sQuery(id+"F7.wireOp",EDGE,"E75.bottom")}),-1.0]])]});
            var Q3;
            Q3=makeQuery(id+"F7.imprint","IMPRINT",FACE,{"disambiguationData":[TD([[makeQuery(id+"F7.imprint","IMPRINT",EDGE,{"derivedFrom":sQuery(id+"F7.wireOp",EDGE,"E76.bottom")}),-1.0]])]});
            extrude(context, id + "F14", {"entities" : qUnion([Q0, Q1, Q2, Q3]), "operationType" : NewBodyOperationType.REMOVE, "oppositeDirection" : true, "depth" : 12.7 * mm, "offsetDistance" : 25.4 * mm});
        }
        {
            var Q0;
            Q0=makeQuery(id+"F10.imprint","IMPRINT",FACE,{"disambiguationData":[TD([[makeQuery(id+"F10.imprint","IMPRINT",EDGE,{"derivedFrom":sQuery(id+"F10.wireOp",EDGE,"E79.bottom")}),-1.0]])]});
            extrude(context, id + "F15", {"entities" : qUnion([Q0]), "operationType" : NewBodyOperationType.REMOVE, "oppositeDirection" : true, "depth" : 12.7 * mm, "offsetDistance" : 25.4 * mm});
        }
        {
            var Q0;
            Q0=makeQuery(id+"F9.imprint","IMPRINT",FACE,{"disambiguationData":[TD([[makeQuery(id+"F9.imprint","IMPRINT",EDGE,{"derivedFrom":sQuery(id+"F9.wireOp",EDGE,"E78.bottom")}),-1.0]])]});
            extrude(context, id + "F16", {"entities" : qUnion([Q0]), "operationType" : NewBodyOperationType.REMOVE, "oppositeDirection" : true, "depth" : 25.4 * mm, "offsetDistance" : 25.4 * mm});
        }
        {
            var Q0;
            Q0=makeQuery(id+"F8.imprint","IMPRINT",FACE,{"disambiguationData":[TD([[makeQuery(id+"F8.imprint","IMPRINT",EDGE,{"derivedFrom":sQuery(id+"F8.wireOp",EDGE,"E77.bottom")}),1.0]])]});
            extrude(context, id + "F17", {"entities" : qUnion([Q0]), "operationType" : NewBodyOperationType.REMOVE, "oppositeDirection" : true, "depth" : 12.7 * mm, "offsetDistance" : 25.4 * mm});
        }
    });
